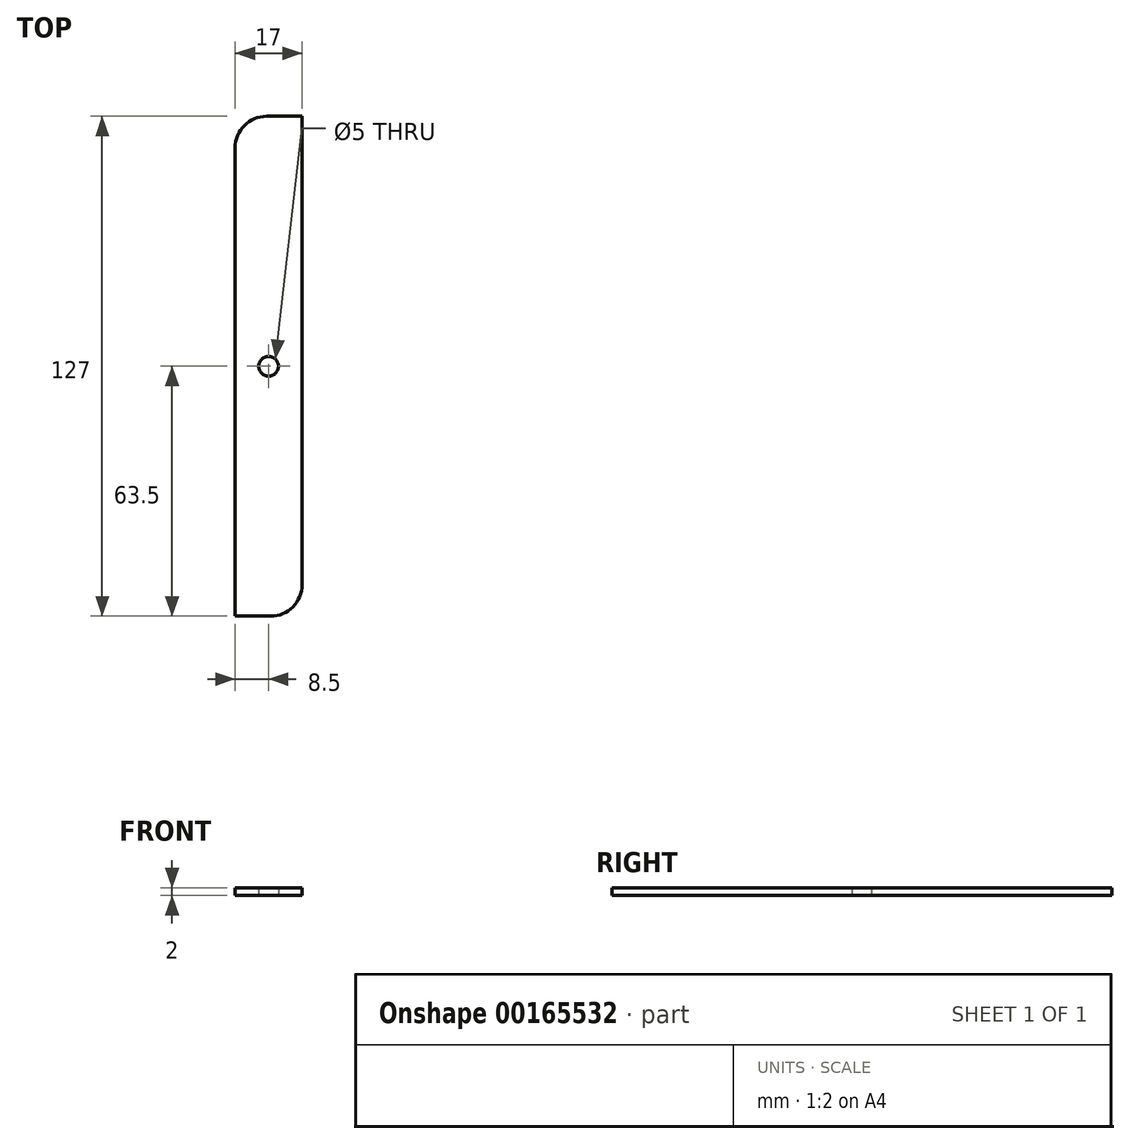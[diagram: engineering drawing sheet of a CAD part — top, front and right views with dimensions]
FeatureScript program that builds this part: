
annotation { "Feature Type Name" : "Feature", "Feature Type Description" : "" }
export const myFeature = defineFeature(function(context is Context, id is Id, definition is map)
    precondition{}
    {
        {
            var Q0;
            Q0=qCreatedBy(makeId("Top.planeOp"),FACE);
            var sketch = newSketch(context, id + "F0", { "sketchPlane" : qUnion([Q0])});
            skLineSegment(sketch, "E0.bottom", {"start": v(-8.5, 63.5) * mm, "end": v(8.5, 63.5) * mm});
            skLineSegment(sketch, "E0.top", {"start": v(-8.5, -63.5) * mm, "end": v(8.5, -63.5) * mm});
            skLineSegment(sketch, "E0.left", {"start": v(-8.5, 63.5) * mm, "end": v(-8.5, -63.5) * mm});
            skLineSegment(sketch, "E0.right", {"start": v(8.5, 63.5) * mm, "end": v(8.5, -63.5) * mm});
            skPoint(sketch, "E0.middle", {"position": v(0, 0) * mm});
            skCircle(sketch, "E1", {"center": v(0, 0) * mm, "radius": 2.5 * mm});
            skSolve(sketch);
        }
        {
            var Q0;
            Q0=makeQuery(id+"F0.imprint","IMPRINT",FACE,{"disambiguationData":[TD([[makeQuery(id+"F0.imprint","IMPRINT",EDGE,{"derivedFrom":sQuery(id+"F0.wireOp",EDGE,"E0.bottom")}),-1.0]])]});
            extrude(context, id + "F1", {"entities" : qUnion([Q0]), "depth" : 2 * mm});
        }
        {
            var Q0;
            Q0=makeQuery(id+"F1.opExtrude","SWEPT_EDGE",EDGE,{"disambiguationData":[OSD([sQuery(id+"F0.wireOp",EDGE,"E0.bottom"),sQuery(id+"F0.wireOp",EDGE,"E0.left")])]});
            var Q1;
            Q1=makeQuery(id+"F1.opExtrude","SWEPT_EDGE",EDGE,{"disambiguationData":[OSD([sQuery(id+"F0.wireOp",EDGE,"E0.top"),sQuery(id+"F0.wireOp",EDGE,"E0.right")])]});
            fillet(context, id + "F2", {"entities" : qUnion([Q0, Q1]), "radius" : 8 * mm, "tangentPropagation" : true, "allowEdgeOverflow" : false});
        }
    });
